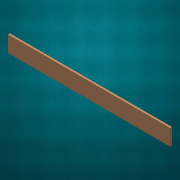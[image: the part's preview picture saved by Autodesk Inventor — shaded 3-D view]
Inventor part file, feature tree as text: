
AUTODESK INVENTOR PART (.ipt)
format: ipt  version: 2017 (Build 210142000, 142)  size: 110,080 bytes
history: native  units: in
note: dims shown in document units (in); Inventor stores cm internally (conversion verified against a paired STEP export)
features: extrude x1, sketch x1
ambient origin geometry x8: Origin, YZ Plane, XZ Plane, XY Plane, X Axis, Y Axis, Z Axis, Center Point
bodies: Solid1 (feature_tree)
feature tree (2):
  extrude  "Extrusion1"  Depth=8.0in
  sketch  "Sketch1"  dims[d0=0.875in d1=8.0in d2=79.875in d3=0.0in]
